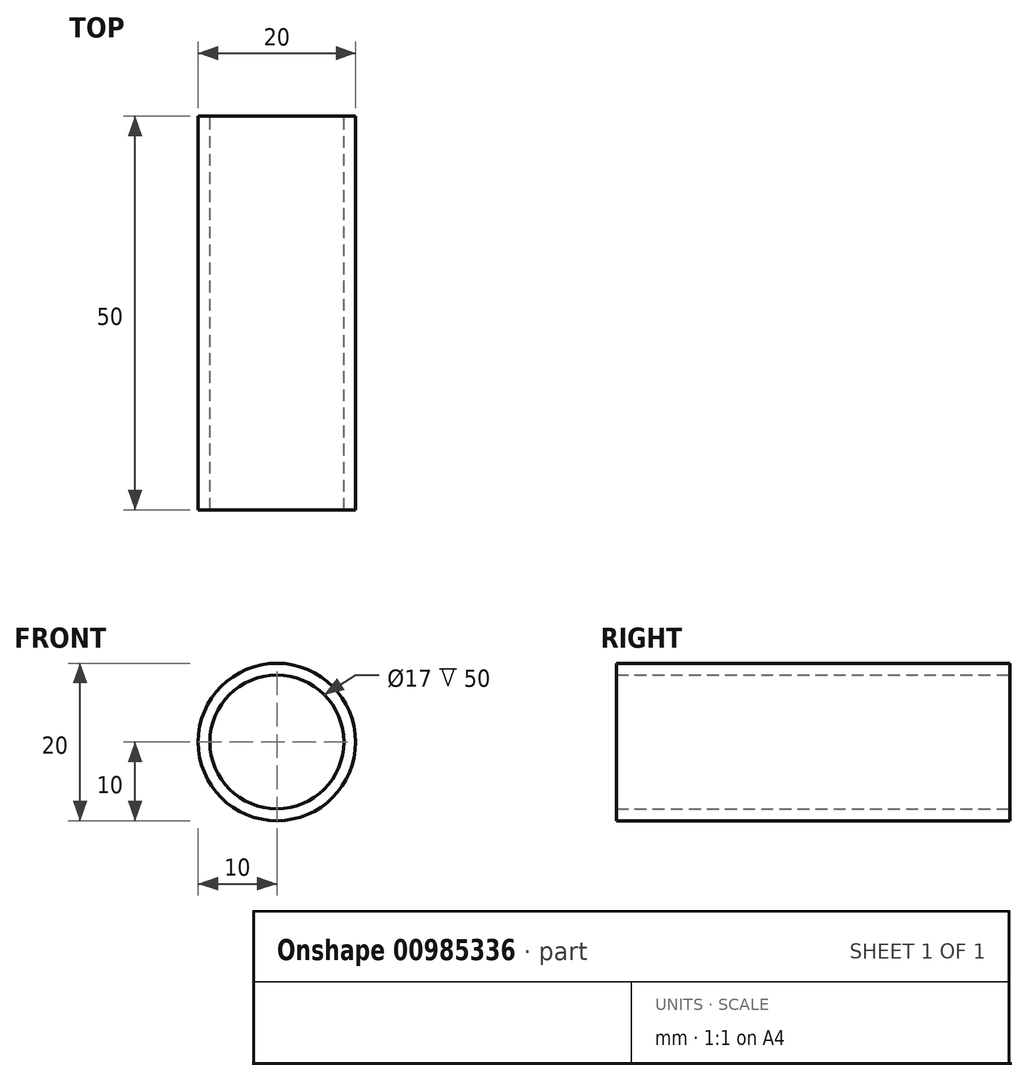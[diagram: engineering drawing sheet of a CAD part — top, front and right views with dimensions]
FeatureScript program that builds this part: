
annotation { "Feature Type Name" : "Feature", "Feature Type Description" : "" }
export const myFeature = defineFeature(function(context is Context, id is Id, definition is map)
    precondition{}
    {
        {
            var Q0;
            Q0=qCreatedBy(makeId("Front.planeOp"),FACE);
            var sketch = newSketch(context, id + "F0", { "sketchPlane" : qUnion([Q0])});
            skCircle(sketch, "E0", {"center": v(0, 0) * mm, "radius": 10 * mm});
            skCircle(sketch, "E1", {"center": v(0, 0) * mm, "radius": 8.5 * mm});
            skSolve(sketch);
        }
        {
            var Q0;
            Q0=makeQuery(id+"F0.imprint","IMPRINT",FACE,{"disambiguationData":[TD([[makeQuery(id+"F0.imprint","IMPRINT",EDGE,{"derivedFrom":sQuery(id+"F0.wireOp",EDGE,"E0")}),1.0]])]});
            extrude(context, id + "F1", {"entities" : qUnion([Q0]), "endBound" : BoundingType.SYMMETRIC, "depth" : 50 * mm});
        }
    });
